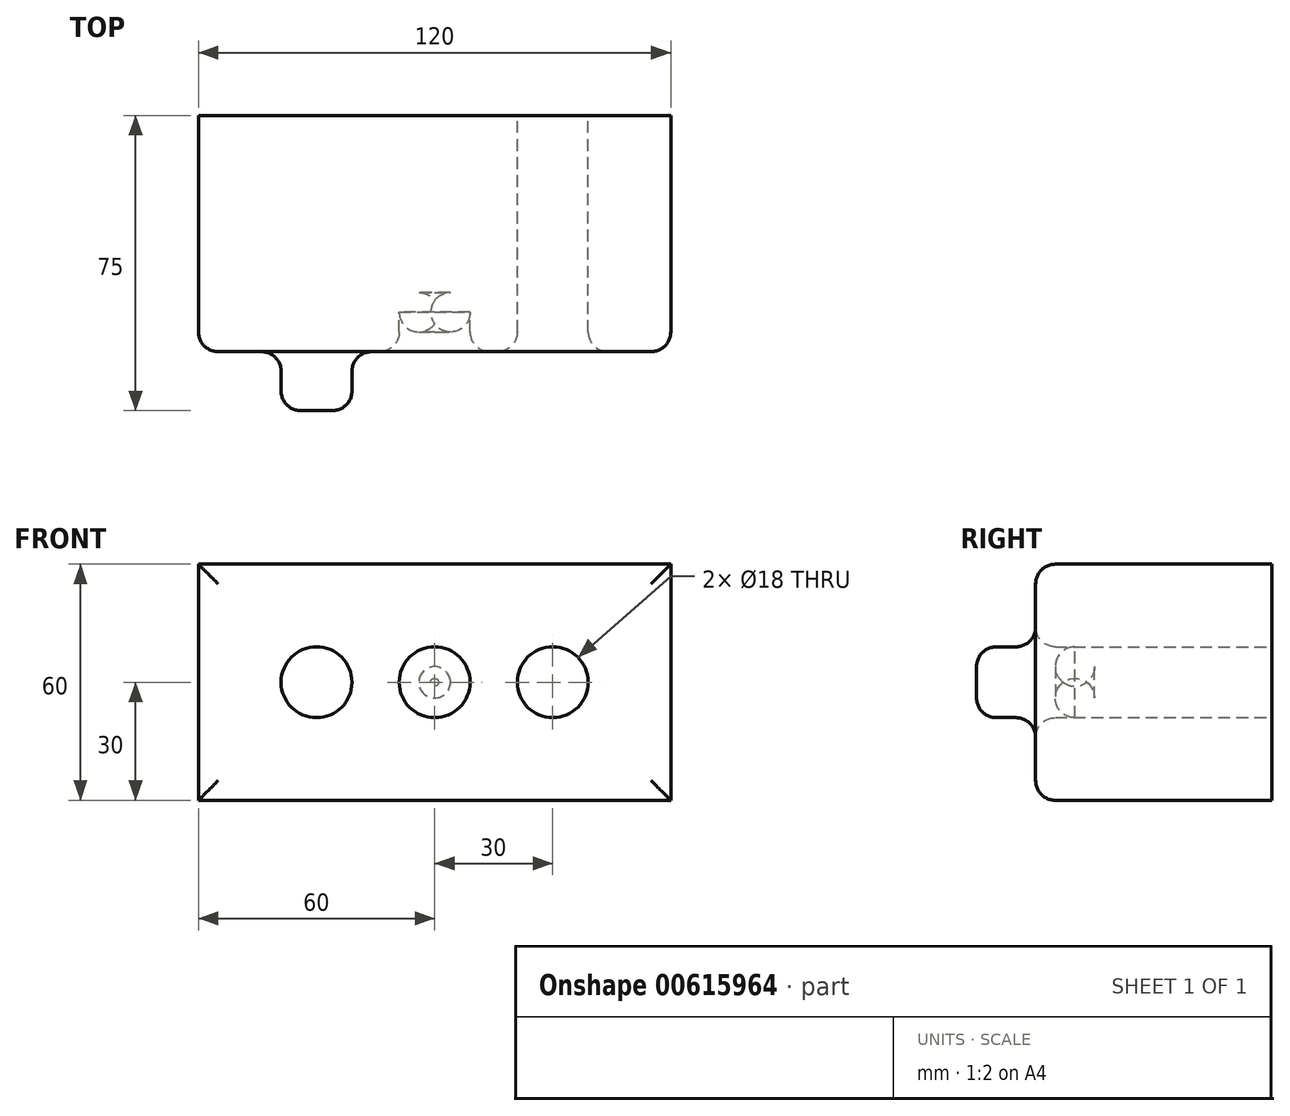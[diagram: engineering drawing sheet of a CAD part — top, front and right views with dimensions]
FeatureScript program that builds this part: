
annotation { "Feature Type Name" : "Feature", "Feature Type Description" : "" }
export const myFeature = defineFeature(function(context is Context, id is Id, definition is map)
    precondition{}
    {
        {
            var Q0;
            Q0=qCreatedBy(makeId("Front.planeOp"),FACE);
            var sketch = newSketch(context, id + "F0", { "sketchPlane" : qUnion([Q0])});
            skLineSegment(sketch, "E0.bottom", {"start": v(0, 0) * mm, "end": v(120, 0) * mm});
            skLineSegment(sketch, "E0.top", {"start": v(0, 30) * mm, "end": v(120, 30) * mm});
            skLineSegment(sketch, "E0.left", {"start": v(0, 0) * mm, "end": v(0, 30) * mm});
            skLineSegment(sketch, "E0.right", {"start": v(120, 0) * mm, "end": v(120, 30) * mm});
            skCircle(sketch, "E1", {"center": v(30, 0) * mm, "radius": 9 * mm});
            skCircle(sketch, "E2", {"center": v(60, 0) * mm, "radius": 9 * mm});
            skCircle(sketch, "E3", {"center": v(90, 0) * mm, "radius": 9 * mm});
            skLineSegment(sketch, "E4.top", {"start": v(0, -30) * mm, "end": v(120, -30) * mm});
            skLineSegment(sketch, "E4.left", {"start": v(0, 0) * mm, "end": v(0, -30) * mm});
            skLineSegment(sketch, "E4.right", {"start": v(120, 0) * mm, "end": v(120, -30) * mm});
            skLineSegment(sketch, "E5.left", {"start": v(120, 30) * mm, "end": v(120, 30) * mm});
            skLineSegment(sketch, "E5.right", {"start": v(4828.16, 30) * mm, "end": v(4828.16, 30) * mm});
            skLineSegment(sketch, "E6.bottom", {"start": v(4049.3, 30) * mm, "end": v(3611.17, 30) * mm});
            skSolve(sketch);
        }
        {
            var Q0;
            Q0 = qSketchRegion(id + "F0", true);
            extrude(context, id + "F1", {"entities" : qUnion([Q0]), "depth" : 60 * mm, "offsetDistance" : 25 * mm});
        }
        {
            var Q0;
            Q0=qCreatedBy(makeId("Front.planeOp"),FACE);
            var sketch = newSketch(context, id + "F2", { "sketchPlane" : qUnion([Q0])});
            skLineSegment(sketch, "E7", {"start": v(0, 0) * mm, "end": v(30, 0) * mm});
            skLineSegment(sketch, "E8", {"start": v(30, 0) * mm, "end": v(60, 0) * mm});
            skLineSegment(sketch, "E9", {"start": v(60, 0) * mm, "end": v(90, 0) * mm});
            skCircle(sketch, "E10", {"center": v(30, 0) * mm, "radius": 9 * mm});
            skCircle(sketch, "E11", {"center": v(60, 0) * mm, "radius": 9 * mm});
            skCircle(sketch, "E12", {"center": v(90, 0) * mm, "radius": 9 * mm});
            skSolve(sketch);
        }
        {
            var Q0;
            {var subQ0=sQuery(id+"F2.wireOp",EDGE,"E8");var subQ1=sQuery(id+"F2.wireOp",EDGE,"E7");var subQ2=makeQuery(id+"F2.imprint","INTERSECT",VERTEX,{"derivedFrom":[subQ1,subQ0]});Q0=makeQuery(id+"F2.imprint","IMPRINT",FACE,{"disambiguationData":[TD([[makeQuery(id+"F2.imprint","IMPRINT",EDGE,{"disambiguationData":[TD([[subQ2,1.0]])],"derivedFrom":subQ1}),1.0]])]});}
            var Q1;
            {var subQ0=sQuery(id+"F2.wireOp",EDGE,"E8");var subQ1=sQuery(id+"F2.wireOp",EDGE,"E7");var subQ2=makeQuery(id+"F2.imprint","INTERSECT",VERTEX,{"derivedFrom":[subQ1,subQ0]});Q1=makeQuery(id+"F2.imprint","IMPRINT",FACE,{"disambiguationData":[TD([[makeQuery(id+"F2.imprint","IMPRINT",EDGE,{"disambiguationData":[TD([[subQ2,1.0]])],"derivedFrom":subQ1}),-1.0]])]});}
            extrude(context, id + "F3", {"entities" : qUnion([Q0, Q1]), "operationType" : NewBodyOperationType.ADD, "depth" : 75 * mm, "offsetDistance" : 25 * mm});
        }
        {
            var Q0;
            {var subQ0=sQuery(id+"F2.wireOp",EDGE,"E9");var subQ1=sQuery(id+"F2.wireOp",EDGE,"E8");var subQ2=makeQuery(id+"F2.imprint","INTERSECT",VERTEX,{"derivedFrom":[subQ1,subQ0]});Q0=makeQuery(id+"F2.imprint","IMPRINT",FACE,{"disambiguationData":[TD([[makeQuery(id+"F2.imprint","IMPRINT",EDGE,{"disambiguationData":[TD([[subQ2,1.0]])],"derivedFrom":subQ1}),1.0]])]});}
            var Q1;
            {var subQ0=sQuery(id+"F2.wireOp",EDGE,"E9");var subQ1=sQuery(id+"F2.wireOp",EDGE,"E8");var subQ2=makeQuery(id+"F2.imprint","INTERSECT",VERTEX,{"derivedFrom":[subQ1,subQ0]});Q1=makeQuery(id+"F2.imprint","IMPRINT",FACE,{"disambiguationData":[TD([[makeQuery(id+"F2.imprint","IMPRINT",EDGE,{"disambiguationData":[TD([[subQ2,1.0]])],"derivedFrom":subQ1}),-1.0]])]});}
            extrude(context, id + "F4", {"entities" : qUnion([Q0, Q1]), "operationType" : NewBodyOperationType.ADD, "depth" : 45 * mm, "offsetDistance" : 25 * mm});
        }
        {
            var Q0;
            Q0=makeQuery(id+"F1.opExtrude","CAP_FACE",FACE,{"disambiguationData":[OSD([sQuery(id+"F0.wireOp",EDGE,"E0.top"),sQuery(id+"F0.wireOp",EDGE,"E0.left"),sQuery(id+"F0.wireOp",EDGE,"E0.right"),sQuery(id+"F0.wireOp",EDGE,"E1"),sQuery(id+"F0.wireOp",EDGE,"E2"),sQuery(id+"F0.wireOp",EDGE,"E3"),sQuery(id+"F0.wireOp",EDGE,"E4.top"),sQuery(id+"F0.wireOp",EDGE,"E4.left"),sQuery(id+"F0.wireOp",EDGE,"E4.right")])],"isStart":false});
            fillet(context, id + "F5", {"entities" : qUnion([Q0]), "radius" : 5 * mm, "tangentPropagation" : true, "allowEdgeOverflow" : false});
        }
        {
            var Q0;
            Q0=makeQuery(id+"F3.opExtrude","CAP_FACE",FACE,{"disambiguationData":[OSD([sQuery(id+"F2.wireOp",EDGE,"E10")])],"isStart":false});
            fillet(context, id + "F6", {"entities" : qUnion([Q0]), "radius" : 5 * mm, "tangentPropagation" : true, "allowEdgeOverflow" : false});
        }
        {
            var Q0;
            Q0=makeQuery(id+"F4.opExtrude","CAP_FACE",FACE,{"disambiguationData":[OSD([sQuery(id+"F2.wireOp",EDGE,"E11")])],"isStart":false});
            fillet(context, id + "F7", {"entities" : qUnion([Q0]), "radius" : 5 * mm, "tangentPropagation" : true, "allowEdgeOverflow" : false});
        }
    });
